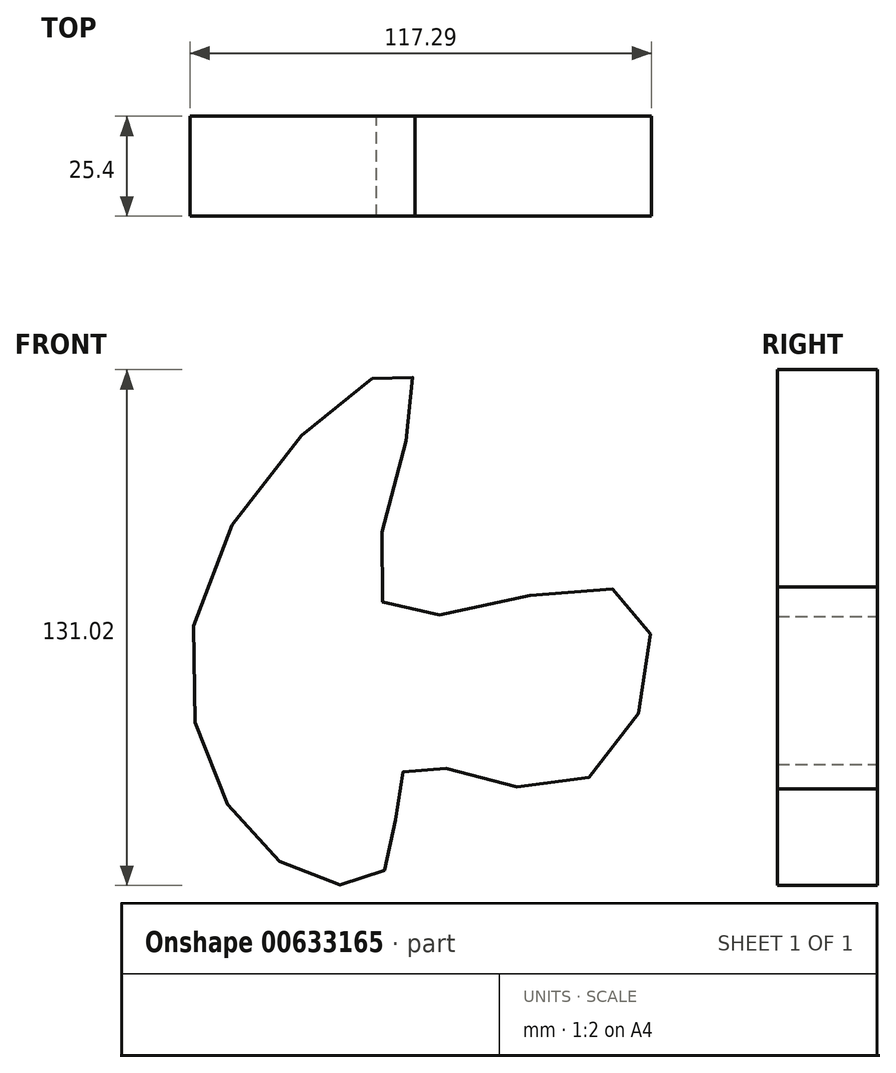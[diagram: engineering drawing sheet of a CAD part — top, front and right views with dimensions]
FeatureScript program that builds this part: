
annotation { "Feature Type Name" : "Feature", "Feature Type Description" : "" }
export const myFeature = defineFeature(function(context is Context, id is Id, definition is map)
    precondition{}
    {
        {
            var Q0;
            Q0=qCreatedBy(makeId("Front.planeOp"),FACE);
            var sketch = newSketch(context, id + "F0", { "sketchPlane" : qUnion([Q0])});
            skFitSpline(sketch, "E0", {"points": [v(-44.66, -58.88) * mm, v(-62.64, 14.75) * mm, v(-10.98, 64.32) * mm, v(-17.88, 6.17) * mm, v(44.03, 8.68) * mm, v(31.9, -38.59) * mm, v(-12.24, -35.03) * mm, v(-17.26, -59.92) * mm, v(-44.66, -58.88) * mm]});
            skSolve(sketch);
        }
        {
            var Q0;
            Q0=makeQuery(id+"F0.imprint","IMPRINT",FACE,{"disambiguationData":[TD([[makeQuery(id+"F0.imprint","IMPRINT",EDGE,{"derivedFrom":sQuery(id+"F0.wireOp",EDGE,"E0")}),-1.0]])]});
            extrude(context, id + "F1", {"entities" : qUnion([Q0]), "depth" : 25.4 * mm, "offsetDistance" : 25.4 * mm});
        }
    });
